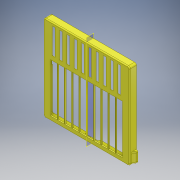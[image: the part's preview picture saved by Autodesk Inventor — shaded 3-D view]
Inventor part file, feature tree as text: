
AUTODESK INVENTOR PART (.ipt)
format: ipt  version: 2017 (Build 210142000, 142)  size: 821,760 bytes
history: native  units: mm
features: move_body x20, direct_edit x12, fillet x11, extrude x10, sketch x10, mirror x2, pattern_linear x2, plane x1, projected_geometry x1
ambient origin geometry x8: Origin, YZ Plane, XZ Plane, XY Plane, X Axis, Y Axis, Z Axis, Center Point
bodies: Solid1 (feature_tree)
feature tree (69):
  extrude  "Extrusion1"  Depth=90.0mm
  extrude  "Extrusion2"  Depth=3.0mm
  extrude  "Extrusion3"  Depth=3.0mm
  fillet  "Fillet1"  [1 undecoded]
  fillet  "Fillet2"  Radius=6.0mm
  extrude  "Extrusion4"  Depth=10.0mm
  direct_edit  "Direct Edit1"
  direct_edit  "Direct Edit2"
  direct_edit  "Direct Edit3"
  direct_edit  "Direct Edit4"
  extrude  "Extrusion5"  Depth=56.0mm
  fillet  "Fillet3"  Radius=86.0mm
  direct_edit  "Direct Edit5"
  extrude  "Extrusion6"  Depth=2.0mm TaperAngle=0.0deg
  direct_edit  "Direct Edit6"
  direct_edit  "Direct Edit7"
  direct_edit  "Direct Edit8"
  fillet  "Fillet4"  Radius=1.5mm
  fillet  "Fillet5"  Radius=4.0mm
  direct_edit  "Direct Edit9"
  direct_edit  "Direct Edit10"
  fillet  "Fillet6"  Radius=2.0mm
  extrude  "Extrusion7"  Depth=4.0mm
  fillet  "Fillet7"  Radius=4.0mm
  direct_edit  "Direct Edit12"
  direct_edit  "Direct Edit13"
  extrude  "Extrusion8"  TaperAngle=0.0deg  [1 undecoded]
  plane  "Work Plane1"
  mirror  "Mirror1"
  extrude  "Extrusion9"  TaperAngle=0.0deg  [1 undecoded]
  fillet  "Fillet10"  [1 undecoded]
  fillet  "Fillet11"  Radius=1.0mm
  fillet  "Fillet12"  Radius=3.0mm
  mirror  "Mirror2"
  extrude  "Extrusion10"  Depth=1.0mm TaperAngle=0.0deg
  pattern_linear  "Rectangular Pattern1"  Spacing1=87.0mm  [1 undecoded]
  pattern_linear  "Rectangular Pattern2"  Spacing1=1.0mm  [1 undecoded]
  fillet  "Fillet13"  Radius=1.0mm
  sketch  "Sketch1"  dims[d0=90.0mm d1=90.0mm]
  sketch  "Sketch2"  dims[d2=3.0mm d3=27.0mm]
  sketch  "Sketch3"  dims[d4=100.0mm d6=7.62mm d7=10.0mm d9=10.0mm d11=3.0mm d12=90.0deg d13=6.0mm]
  projected_geometry  "Projected Loop2"
  sketch  "Sketch4"  dims[d14=50.0mm d15=100.0mm d17=7.62mm d18=10.0mm d20=10.0mm]
  sketch  "Sketch6"  dims[d22=0.5mm d23=0.0mm d24=56.0mm d25=86.0mm]
  sketch  "Sketch7"  dims[d26=90.0deg d27=1.5mm d28=0.0mm d29=1.5mm d30=4.0mm d31=0.0mm d32=2.0mm]
  sketch  "Sketch8"  dims[d33=1.0mm d34=6.0mm d35=4.0mm]
  sketch  "Sketch10"  dims[d36=19.25mm d37=0.0mm d38=0.0mm d39=0.0mm d40=-10.0mm]
  sketch  "Sketch11"  dims[d41=0.0mm d42=0.0mm d43=5.5mm d44=0.0mm d45=0.0mm d46=-5.5mm]
  sketch  "Sketch12"  dims[d47=0.0mm d48=0.0mm d49=4.0mm d50=0.0mm d51=0.0mm d52=-2.5mm d53=1.0mm d54=0.0mm d55=3.0mm d56=0.0mm d57=0.0mm d58=0.5mm d61=87.0mm d62=1.0mm d63=1.0mm d64=1.0mm d65=20.0mm d66=0.5mm d67=0.0mm d68=0.0mm d69=0.0mm d70=1.0mm d71=0.0mm d72=0.0mm d73=0.5mm d74=0.0mm d75=0.0mm d76=25.0mm d77=0.0mm d78=0.0mm d79=-10.0mm d80=0.0mm d81=0.0mm d82=9.0mm d83=0.0mm d84=0.0mm d85=0.1mm d86=0.0mm d87=0.0mm d88=0.1mm d89=0.0mm d90=0.0mm d91=0.25mm d92=1.0mm d93=1.0mm d94=0.0mm d95=0.0mm d96=-0.25mm d97=0.0mm d98=0.0mm d99=0.75mm d100=0.0mm d101=0.0mm d102=-1.0mm d103=1.0mm d104=4.0mm d105=2.0mm d106=4.0mm d107=2.0mm d108=3.0mm d109=0.0mm d113=1.0mm d114=0.0mm d115=0.0mm d116=2.5mm d117=0.0mm d118=0.0mm d119=-1.75mm d120=0.0mm d121=0.0mm d122=-0.6mm d123=3.5mm d124=12.0mm d125=1.5mm d126=0.0mm d129=14.0mm d130=4.0mm d131=2.0mm d132=0.0mm d133=1.0mm d134=2.0mm d135=5.0mm d140=2.0mm d141=-3.490659mm d142=100.0mm d144=7.6mm d145=20.0mm d147=25.0mm d148=1.0mm]
  move_body  "Move1"
  move_body  "Move2"
  move_body  "Move3"
  move_body  "Move4"
  move_body  "Move5"
  move_body  "Move6"
  move_body  "Move7"
  move_body  "Move8"
  move_body  "Move9"
  move_body  "Move10"
  move_body  "Move11"
  move_body  "Move12"
  move_body  "Move13"
  move_body  "Move14"
  move_body  "Move15"
  move_body  "Move16"
  move_body  "Move17"
  move_body  "Move19"
  move_body  "Move20"
  move_body  "Move21"
note: 6 required parameter values undecoded (feature->parameter linkage not recoverable at this tier; creation-order binding heuristic only, values carry confidence <= 0.55)
